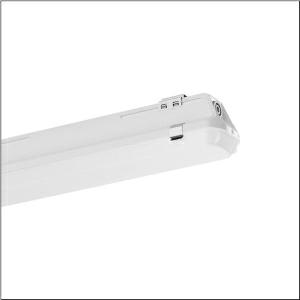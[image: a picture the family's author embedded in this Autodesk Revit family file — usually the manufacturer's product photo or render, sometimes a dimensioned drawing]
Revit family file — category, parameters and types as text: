
# Revit family: monsun_r__11_chemical_51fp30mp480h_0948
name_source: partatom
category: Lighting Fixtures
units: mm (PartAtom-declared; Revit-internal decimal feet)

## family parameters
Cut with Voids When Loaded = No
Host = Face
Light Source = No
Part Type = Normal
Room Calculation Point = No
Round Connector Dimension = Use Diameter
Shared = No

## types (1)
- --- (1 x LED, 7640 lm, 45.4 W, 4000K)
    Apparent Load = 45 VA
    CIE Flux Codes = 48 77 93 95 100
    Color Rendering = 80
    Color Temperature = 4000K
    Default Elevation = 1800 mm
    Description = Monsun® 11 chemical, damp-proof luminaire, chain hanger, primary optical cover: enclosure, of PA, light emission: direct distribution, primary light characteristic: symmetric, installation type: suspended mounting, surface-mounted, horizontal mounting, vertical mounting, LED, rated luminous flux: 7.640lm, luminous efficacy: 168lm/W, light colour: 840, colour temperature: 4000K, control gear: ECG, with terminal, 3-pole, max. 2.5mm², mains connection: 220..240V, AC, 50/60Hz, rated input power: 45W, luminaire housing, of glass-fibre reinforced polyester, uncoated, bright grey, incl. chain hanger, length: 1.590mm, width: 90mm, height: 88mm, clip for enclosure, of stainless steel (V2A), ceiling mounting element, of stainless steel (V2A), chain hanger, of stainless steel (V2A), protection rating (complete): IP66, insulation class (complete): insulation class I (protective earthing), certification: CE, ENEC, VDE, UKCA, protection symbol: D, impact resistance: IK08, permissible operating ambient temperature: -35..+40°C, standard: EN 50419, EN 60598-2-1, no direct snow, no direct sun, no direct rain, for indoor or canopied outdoor use, corresponds to IFS (International Featured Standards) requirements for safety and quality in the food industry, contact your sales advisor before using the luminaires in applications with unclear chemical exposure, large temperature fluctuations or condensation-forming humidity, LABS conformity tested according to VDMA 24364:2018-05, packaging unit: 1 piece
    Height = 89 mm
    Lamp = 1 x LED
    Lamp Light Flux = 7640 lm
    Lamp Power = 45.4 W
    Lamp count = 1
    Length = 1590 mm
    Luminous efficacy = 168 lm/W
    Manufacturer = Siteco
    ModVariant = No
    Model = 51FP30MP480H
    Mounting Place = Ceiling
    Mounting Type = Surface mounted
    Number of Poles = 1
    OnlyDefault = Yes
    Power Factor = 1
    Product Name = Monsun® 11 chemical
    Product group = damp-proof luminaire
    ProductGroupID = 300
    Protection Class = Protection class I
    Protection Degree = IP 66
    RLX_Detail_Level = 1
    RLX_Emergency_Light_Flux = 0 lm
    RLX_Emergency_Type = 0
    RLX_Emergency_Type_DB = No
    RlxData = <blob elided: 89997 chars, md5=925bcb97>
    Socket = socket
    Standby Power = 0 W
    System Light Flux = 7640 lm
    System Power = 45 W
    Type Comments = factory setting: luminous flux: 100 % | (A | C | E) | 105 mA
    Type Image = l_1004748.jpg
    URL = http://relux.com
    VarID = @adj_142167
    Voltage = 0 V
    Weight = 0.00 kg
    Width = 90 mm

## geometry (parser evidence)
native form markers: Blend x4, Sweep x11
no freeform markers — native parametric forms only
